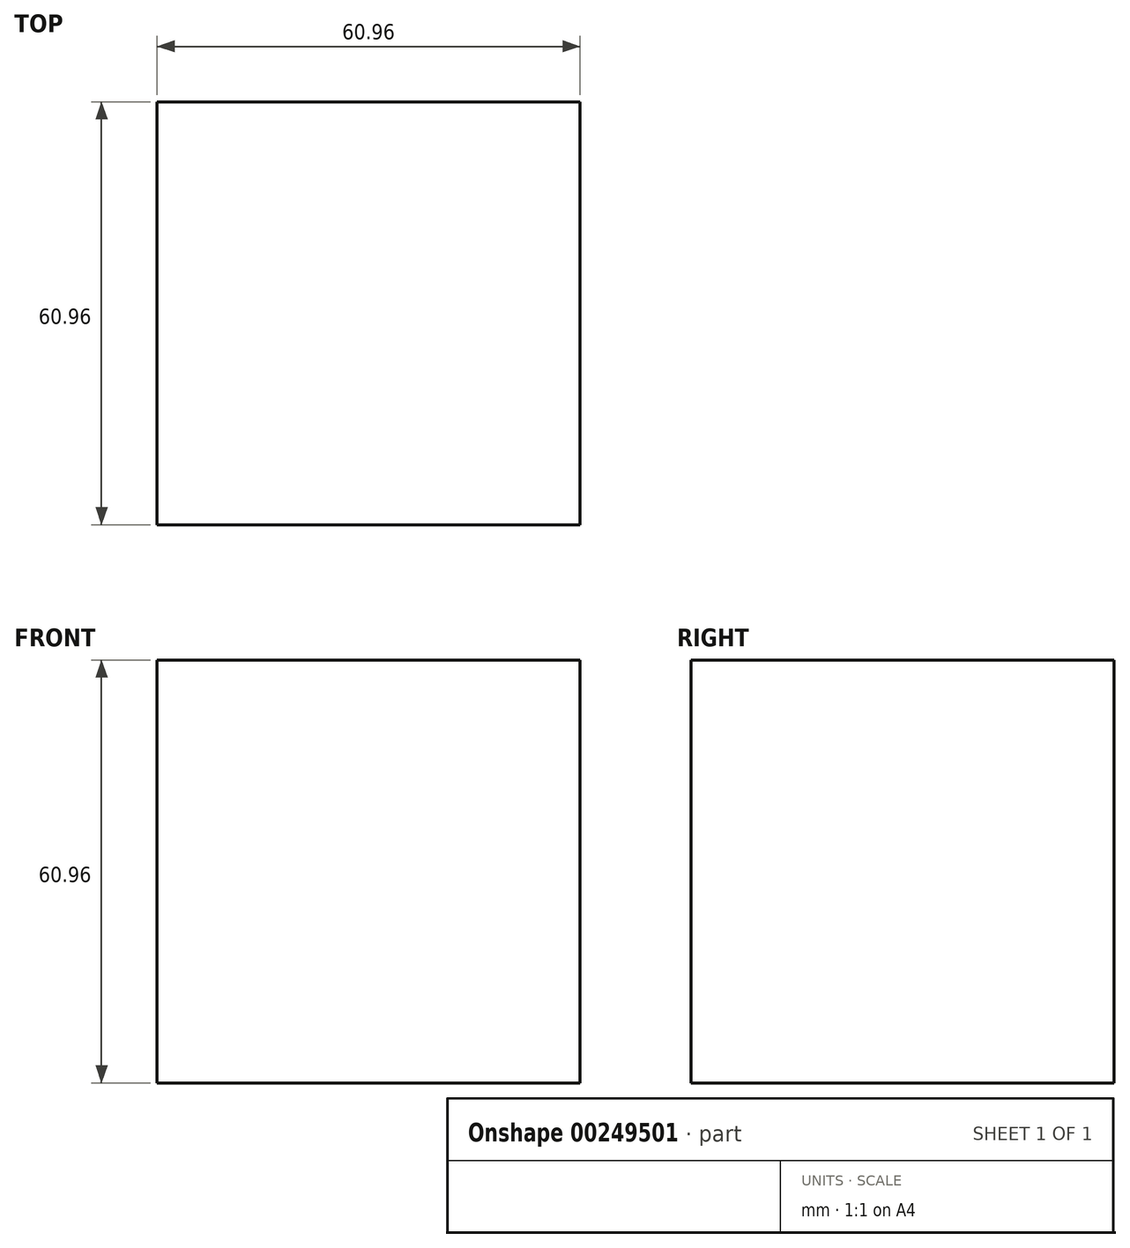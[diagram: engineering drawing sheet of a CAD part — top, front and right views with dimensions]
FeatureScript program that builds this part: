
annotation { "Feature Type Name" : "Feature", "Feature Type Description" : "" }
export const myFeature = defineFeature(function(context is Context, id is Id, definition is map)
    precondition{}
    {
        {
            var Q0;
            Q0=qCreatedBy(makeId("Front.planeOp"),FACE);
            var sketch = newSketch(context, id + "F0", { "sketchPlane" : qUnion([Q0])});
            skLineSegment(sketch, "E0.bottom", {"start": v(30.48, 30.48) * mm, "end": v(-30.48, 30.48) * mm});
            skLineSegment(sketch, "E0.top", {"start": v(30.48, -30.48) * mm, "end": v(-30.48, -30.48) * mm});
            skLineSegment(sketch, "E0.left", {"start": v(30.48, 30.48) * mm, "end": v(30.48, -30.48) * mm});
            skLineSegment(sketch, "E0.right", {"start": v(-30.48, 30.48) * mm, "end": v(-30.48, -30.48) * mm});
            skPoint(sketch, "E0.middle", {"position": v(0, 0) * mm});
            skSolve(sketch);
        }
        {
            var Q0;
            Q0=makeQuery(id+"F0.imprint","IMPRINT",FACE,{"disambiguationData":[TD([[makeQuery(id+"F0.imprint","IMPRINT",EDGE,{"derivedFrom":sQuery(id+"F0.wireOp",EDGE,"E0.bottom")}),1.0]])]});
            extrude(context, id + "F1", {"entities" : qUnion([Q0]), "depth" : 60.96 * mm});
        }
    });
